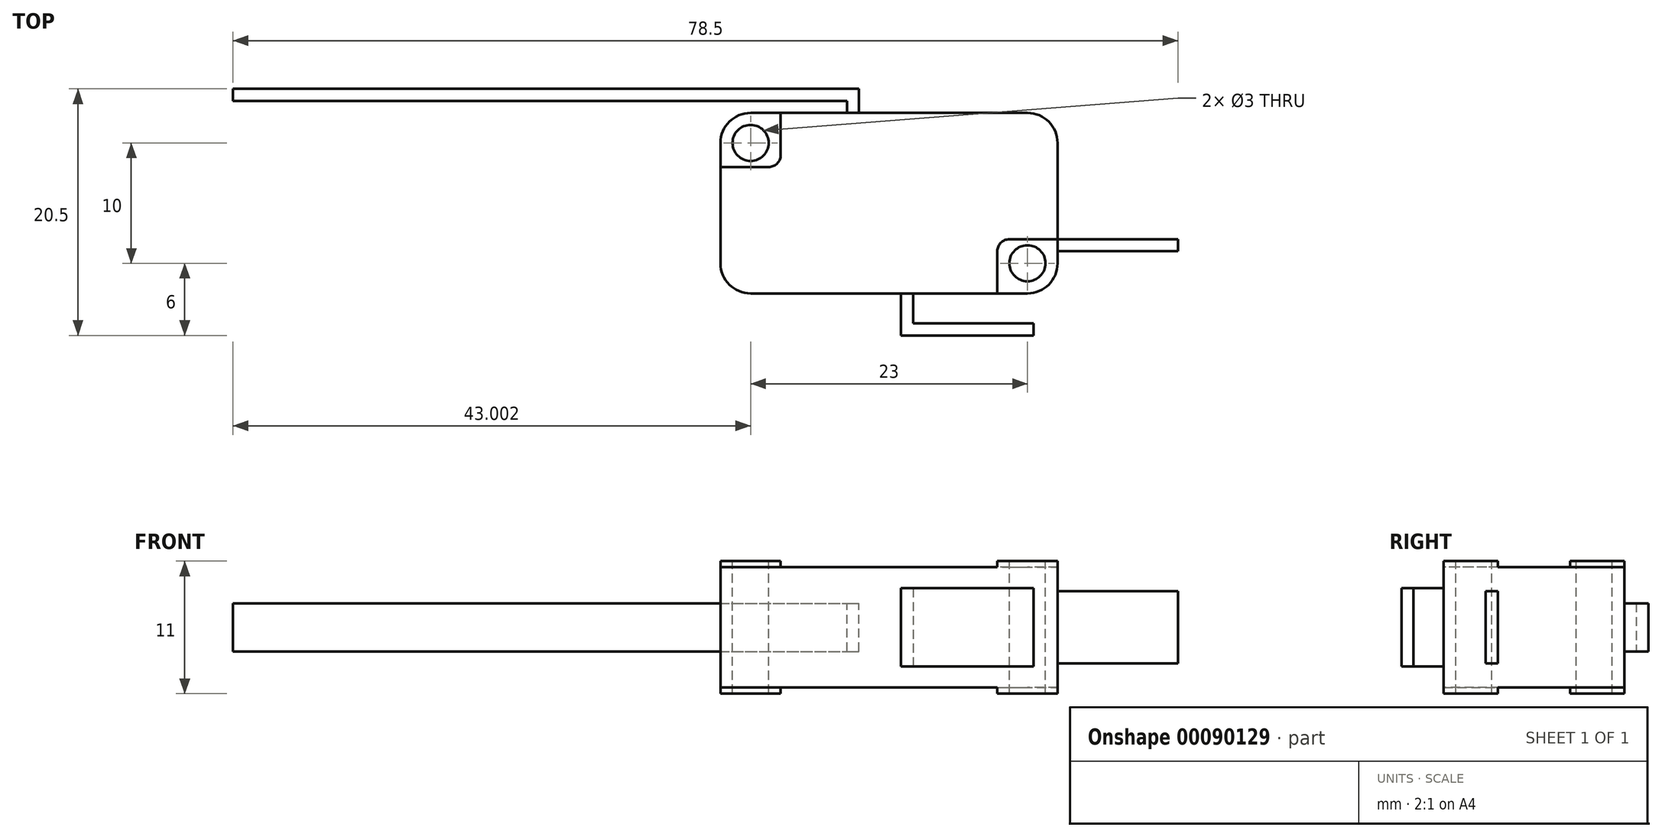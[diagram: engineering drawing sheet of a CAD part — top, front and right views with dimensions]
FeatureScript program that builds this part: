
annotation { "Feature Type Name" : "Feature", "Feature Type Description" : "" }
export const myFeature = defineFeature(function(context is Context, id is Id, definition is map)
    precondition{}
    {
        {
            var Q0;
            Q0=qCreatedBy(makeId("Top.planeOp"),FACE);
            var sketch = newSketch(context, id + "F0", { "sketchPlane" : qUnion([Q0])});
            skLineSegment(sketch, "E0.bottom", {"start": v(-11.85, 4.57) * mm, "end": v(11.15, 4.57) * mm});
            skLineSegment(sketch, "E0.top", {"start": v(-11.85, -10.43) * mm, "end": v(11.15, -10.43) * mm});
            skLineSegment(sketch, "E0.left", {"start": v(-14.35, 2.07) * mm, "end": v(-14.35, -7.93) * mm});
            skLineSegment(sketch, "E0.right", {"start": v(13.65, 2.07) * mm, "end": v(13.65, -7.93) * mm});
            skPoint(sketch, "E1.visualSharp", {"position": v(-14.35, 4.57) * mm});
            skArc(sketch, "E1.filletArc", {"start": v(-11.85, 4.57) * mm, "mid": v(-13.62, 3.84) * mm, "end": v(-14.35, 2.07) * mm});
            skPoint(sketch, "E2.visualSharp", {"position": v(13.65, 4.57) * mm});
            skArc(sketch, "E2.filletArc", {"start": v(13.65, 2.07) * mm, "mid": v(12.92, 3.84) * mm, "end": v(11.15, 4.57) * mm});
            skPoint(sketch, "E3.visualSharp", {"position": v(13.65, -10.43) * mm});
            skArc(sketch, "E3.filletArc", {"start": v(11.15, -10.43) * mm, "mid": v(12.92, -9.7) * mm, "end": v(13.65, -7.93) * mm});
            skPoint(sketch, "E4.visualSharp", {"position": v(-14.35, -10.43) * mm});
            skArc(sketch, "E4.filletArc", {"start": v(-14.35, -7.93) * mm, "mid": v(-13.62, -9.7) * mm, "end": v(-11.85, -10.43) * mm});
            skSolve(sketch);
        }
        {
            var Q0;
            Q0 = qSketchRegion(id + "F0", true);
            extrude(context, id + "F1", {"entities" : qUnion([Q0]), "depth" : 10 * mm});
        }
        {
            var Q0;
            Q0=makeQuery(id+"F1.opExtrude","CAP_FACE",FACE,{"disambiguationData":[OSD([sQuery(id+"F0.wireOp",EDGE,"E0.bottom"),sQuery(id+"F0.wireOp",EDGE,"E0.top"),sQuery(id+"F0.wireOp",EDGE,"E0.left"),sQuery(id+"F0.wireOp",EDGE,"E0.right"),sQuery(id+"F0.wireOp",EDGE,"E1.filletArc"),sQuery(id+"F0.wireOp",EDGE,"E2.filletArc"),sQuery(id+"F0.wireOp",EDGE,"E3.filletArc"),sQuery(id+"F0.wireOp",EDGE,"E4.filletArc")])],"isStart":false});
            var sketch = newSketch(context, id + "F2", { "sketchPlane" : qUnion([Q0])});
            skCircle(sketch, "E5", {"center": v(-11.85, 2.07) * mm, "radius": 1.5 * mm});
            skCircle(sketch, "E6", {"center": v(11.15, -7.93) * mm, "radius": 1.5 * mm});
            skSolve(sketch);
        }
        {
            var Q0;
            Q0 = qSketchRegion(id + "F2", true);
            extrude(context, id + "F3", {"entities" : qUnion([Q0]), "operationType" : NewBodyOperationType.REMOVE, "oppositeDirection" : true, "depth" : 15 * mm});
        }
        {
            var Q0;
            Q0=makeQuery(id+"F1.opExtrude","CAP_FACE",FACE,{"disambiguationData":[OSD([sQuery(id+"F0.wireOp",EDGE,"E0.bottom"),sQuery(id+"F0.wireOp",EDGE,"E0.top"),sQuery(id+"F0.wireOp",EDGE,"E0.left"),sQuery(id+"F0.wireOp",EDGE,"E0.right"),sQuery(id+"F0.wireOp",EDGE,"E1.filletArc"),sQuery(id+"F0.wireOp",EDGE,"E2.filletArc"),sQuery(id+"F0.wireOp",EDGE,"E3.filletArc"),sQuery(id+"F0.wireOp",EDGE,"E4.filletArc")])],"isStart":false});
            var sketch = newSketch(context, id + "F4", { "sketchPlane" : qUnion([Q0])});
            skPoint(sketch, "E7", {"position": v(-9.35, 4.57) * mm});
            skPoint(sketch, "E8", {"position": v(-9.35, 0.07) * mm});
            skLineSegment(sketch, "E9.bottom", {"start": v(-9.35, 4.57) * mm, "end": v(-14.35, 4.57) * mm});
            skLineSegment(sketch, "E9.top", {"start": v(-10.35, 0.07) * mm, "end": v(-14.35, 0.07) * mm});
            skLineSegment(sketch, "E9.left", {"start": v(-9.35, 4.57) * mm, "end": v(-9.35, 1.07) * mm});
            skLineSegment(sketch, "E9.right", {"start": v(-14.35, 4.57) * mm, "end": v(-14.35, 0.07) * mm});
            skPoint(sketch, "E10", {"position": v(8.65, -10.43) * mm});
            skPoint(sketch, "E11", {"position": v(8.65, -5.93) * mm});
            skLineSegment(sketch, "E12.bottom", {"start": v(9.65, -5.93) * mm, "end": v(13.66, -5.93) * mm});
            skLineSegment(sketch, "E12.top", {"start": v(8.65, -10.43) * mm, "end": v(13.66, -10.43) * mm});
            skLineSegment(sketch, "E12.left", {"start": v(8.65, -6.93) * mm, "end": v(8.65, -10.43) * mm});
            skLineSegment(sketch, "E12.right", {"start": v(13.66, -5.93) * mm, "end": v(13.66, -10.43) * mm});
            skArc(sketch, "E13.filletArc", {"start": v(9.65, -5.93) * mm, "mid": v(8.95, -6.22) * mm, "end": v(8.65, -6.93) * mm});
            skArc(sketch, "E14.filletArc", {"start": v(-10.35, 0.07) * mm, "mid": v(-9.64, 0.36) * mm, "end": v(-9.35, 1.07) * mm});
            skSolve(sketch);
        }
        {
            var Q0;
            {var subQ3=sQuery(id+"F4.wireOp",EDGE,"E9.top");Q0=makeQuery(id+"F4.imprint","IMPRINT",FACE,{"disambiguationData":[TD([[makeQuery(id+"F4.imprint","IMPRINT",EDGE,{"derivedFrom":subQ3}),-1.0]])]});}
            var Q1;
            {var subQ3=sQuery(id+"F4.wireOp",EDGE,"E12.left");Q1=makeQuery(id+"F4.imprint","IMPRINT",FACE,{"disambiguationData":[TD([[makeQuery(id+"F4.imprint","IMPRINT",EDGE,{"derivedFrom":subQ3}),1.0]])]});}
            extrude(context, id + "F5", {"entities" : qUnion([Q0, Q1]), "operationType" : NewBodyOperationType.ADD, "depth" : 0.5 * mm});
        }
        {
            var Q0;
            Q0=makeQuery(id+"F1.opExtrude","CAP_FACE",FACE,{"disambiguationData":[OSD([sQuery(id+"F0.wireOp",EDGE,"E0.bottom"),sQuery(id+"F0.wireOp",EDGE,"E0.top"),sQuery(id+"F0.wireOp",EDGE,"E0.left"),sQuery(id+"F0.wireOp",EDGE,"E0.right"),sQuery(id+"F0.wireOp",EDGE,"E1.filletArc"),sQuery(id+"F0.wireOp",EDGE,"E2.filletArc"),sQuery(id+"F0.wireOp",EDGE,"E3.filletArc"),sQuery(id+"F0.wireOp",EDGE,"E4.filletArc")])],"isStart":true});
            var sketch = newSketch(context, id + "F6", { "sketchPlane" : qUnion([Q0])});
            skLineSegment(sketch, "E15.bottom", {"start": v(-14.35, -0.07) * mm, "end": v(-10.35, -0.07) * mm});
            skLineSegment(sketch, "E15.top", {"start": v(-14.35, -4.57) * mm, "end": v(-9.35, -4.57) * mm});
            skLineSegment(sketch, "E15.left", {"start": v(-14.35, -0.07) * mm, "end": v(-14.35, -4.57) * mm});
            skLineSegment(sketch, "E15.right", {"start": v(-9.35, -1.07) * mm, "end": v(-9.35, -4.57) * mm});
            skLineSegment(sketch, "E16.bottom", {"start": v(8.65, 10.43) * mm, "end": v(13.65, 10.43) * mm});
            skLineSegment(sketch, "E16.top", {"start": v(9.65, 5.93) * mm, "end": v(13.65, 5.93) * mm});
            skLineSegment(sketch, "E16.left", {"start": v(8.65, 10.43) * mm, "end": v(8.65, 6.93) * mm});
            skLineSegment(sketch, "E16.right", {"start": v(13.65, 10.43) * mm, "end": v(13.65, 5.93) * mm});
            skPoint(sketch, "E17.visualSharp", {"position": v(8.65, 5.93) * mm});
            skArc(sketch, "E17.filletArc", {"start": v(8.65, 6.93) * mm, "mid": v(8.95, 6.22) * mm, "end": v(9.65, 5.93) * mm});
            skPoint(sketch, "E18.visualSharp", {"position": v(-9.35, -0.07) * mm});
            skArc(sketch, "E18.filletArc", {"start": v(-9.35, -1.07) * mm, "mid": v(-9.64, -0.36) * mm, "end": v(-10.35, -0.07) * mm});
            skSolve(sketch);
        }
        {
            var Q0;
            {var subQ3=sQuery(id+"F6.wireOp",EDGE,"E15.bottom");Q0=makeQuery(id+"F6.imprint","IMPRINT",FACE,{"disambiguationData":[TD([[makeQuery(id+"F6.imprint","IMPRINT",EDGE,{"derivedFrom":subQ3}),-1.0]])]});}
            var Q1;
            {var subQ3=sQuery(id+"F6.wireOp",EDGE,"E16.top");Q1=makeQuery(id+"F6.imprint","IMPRINT",FACE,{"disambiguationData":[TD([[makeQuery(id+"F6.imprint","IMPRINT",EDGE,{"derivedFrom":subQ3}),1.0]])]});}
            extrude(context, id + "F7", {"entities" : qUnion([Q0, Q1]), "operationType" : NewBodyOperationType.ADD, "depth" : 0.5 * mm});
        }
        {
            var Q0;
            {var subQ0=sQuery(id+"F0.wireOp",EDGE,"E0.right");Q0=makeQuery(id+"F7.boolean.opBoolean","MERGE",FACE,{"derivedFrom":[makeQuery(id+"F5.boolean.opBoolean","MERGE",FACE,{"derivedFrom":[makeQuery(id+"F1.opExtrude","SWEPT_FACE",FACE,{"disambiguationData":[OSD([subQ0])]}),makeQuery(id+"F5.opExtrude","SWEPT_FACE",FACE,{"disambiguationData":[OSD([subQ0])]})]}),makeQuery(id+"F7.opExtrude","SWEPT_FACE",FACE,{"disambiguationData":[OSD([sQuery(id+"F6.wireOp",EDGE,"E16.right")])]})]});}
            var sketch = newSketch(context, id + "F8", { "sketchPlane" : qUnion([Q0])});
            skLineSegment(sketch, "E19.bottom", {"start": v(-5.93, 8) * mm, "end": v(-6.93, 8) * mm});
            skLineSegment(sketch, "E19.top", {"start": v(-5.93, 2) * mm, "end": v(-6.93, 2) * mm});
            skLineSegment(sketch, "E19.left", {"start": v(-5.93, 8) * mm, "end": v(-5.93, 2) * mm});
            skLineSegment(sketch, "E19.right", {"start": v(-6.93, 8) * mm, "end": v(-6.93, 2) * mm});
            skSolve(sketch);
        }
        {
            var Q0;
            Q0=makeQuery(id+"F8.imprint","IMPRINT",FACE,{"disambiguationData":[TD([[makeQuery(id+"F8.imprint","IMPRINT",EDGE,{"derivedFrom":sQuery(id+"F8.wireOp",EDGE,"E19.bottom")}),1.0]])]});
            extrude(context, id + "F9", {"entities" : qUnion([Q0]), "operationType" : NewBodyOperationType.ADD, "depth" : 10 * mm});
        }
        {
            var Q0;
            Q0=makeQuery(id+"F7.boolean.opBoolean","MERGE",FACE,{"derivedFrom":[makeQuery(id+"F5.boolean.opBoolean","MERGE",FACE,{"derivedFrom":[makeQuery(id+"F1.opExtrude","SWEPT_FACE",FACE,{"disambiguationData":[OSD([sQuery(id+"F0.wireOp",EDGE,"E0.top")])]}),makeQuery(id+"F5.opExtrude","SWEPT_FACE",FACE,{"disambiguationData":[OSD([sQuery(id+"F4.wireOp",EDGE,"E12.top")])]})]}),makeQuery(id+"F7.opExtrude","SWEPT_FACE",FACE,{"disambiguationData":[OSD([sQuery(id+"F6.wireOp",EDGE,"E16.bottom")])]})]});
            var sketch = newSketch(context, id + "F10", { "sketchPlane" : qUnion([Q0])});
            skLineSegment(sketch, "E20.bottom", {"start": v(0.65, 8.25) * mm, "end": v(1.65, 8.25) * mm});
            skLineSegment(sketch, "E20.top", {"start": v(0.65, 1.75) * mm, "end": v(1.65, 1.75) * mm});
            skLineSegment(sketch, "E20.left", {"start": v(0.65, 8.25) * mm, "end": v(0.65, 1.75) * mm});
            skLineSegment(sketch, "E20.right", {"start": v(1.65, 8.25) * mm, "end": v(1.65, 1.75) * mm});
            skSolve(sketch);
        }
        {
            var Q0;
            Q0=makeQuery(id+"F10.imprint","IMPRINT",FACE,{"disambiguationData":[TD([[makeQuery(id+"F10.imprint","IMPRINT",EDGE,{"derivedFrom":sQuery(id+"F10.wireOp",EDGE,"E20.bottom")}),-1.0]])]});
            extrude(context, id + "F11", {"entities" : qUnion([Q0]), "operationType" : NewBodyOperationType.ADD, "depth" : 3.5 * mm});
        }
        {
            var Q0;
            Q0=makeQuery(id+"F11.opExtrude","SWEPT_FACE",FACE,{"disambiguationData":[OSD([sQuery(id+"F10.wireOp",EDGE,"E20.right")])]});
            var sketch = newSketch(context, id + "F12", { "sketchPlane" : qUnion([Q0])});
            skLineSegment(sketch, "E21.bottom", {"start": v(-13.93, 8.25) * mm, "end": v(-12.93, 8.25) * mm});
            skLineSegment(sketch, "E21.top", {"start": v(-13.93, 1.75) * mm, "end": v(-12.93, 1.75) * mm});
            skLineSegment(sketch, "E21.left", {"start": v(-13.93, 8.25) * mm, "end": v(-13.93, 1.75) * mm});
            skLineSegment(sketch, "E21.right", {"start": v(-12.93, 8.25) * mm, "end": v(-12.93, 1.75) * mm});
            skSolve(sketch);
        }
        {
            var Q0;
            Q0 = qSketchRegion(id + "F12", true);
            extrude(context, id + "F13", {"entities" : qUnion([Q0]), "operationType" : NewBodyOperationType.ADD, "depth" : 10 * mm});
        }
        {
            var Q0;
            Q0=makeQuery(id+"F7.boolean.opBoolean","MERGE",FACE,{"derivedFrom":[makeQuery(id+"F5.boolean.opBoolean","MERGE",FACE,{"derivedFrom":[makeQuery(id+"F1.opExtrude","SWEPT_FACE",FACE,{"disambiguationData":[OSD([sQuery(id+"F0.wireOp",EDGE,"E0.bottom")])]}),makeQuery(id+"F5.opExtrude","SWEPT_FACE",FACE,{"disambiguationData":[OSD([sQuery(id+"F4.wireOp",EDGE,"E9.bottom")])]})]}),makeQuery(id+"F7.opExtrude","SWEPT_FACE",FACE,{"disambiguationData":[OSD([sQuery(id+"F6.wireOp",EDGE,"E15.top")])]})]});
            var sketch = newSketch(context, id + "F14", { "sketchPlane" : qUnion([Q0])});
            skLineSegment(sketch, "E22.bottom", {"start": v(3.85, 3) * mm, "end": v(2.85, 3) * mm});
            skLineSegment(sketch, "E22.top", {"start": v(3.85, 7) * mm, "end": v(2.85, 7) * mm});
            skLineSegment(sketch, "E22.left", {"start": v(3.85, 3) * mm, "end": v(3.85, 7) * mm});
            skLineSegment(sketch, "E22.right", {"start": v(2.85, 3) * mm, "end": v(2.85, 7) * mm});
            skSolve(sketch);
        }
        {
            var Q0;
            Q0 = qSketchRegion(id + "F14", true);
            extrude(context, id + "F15", {"entities" : qUnion([Q0]), "operationType" : NewBodyOperationType.ADD, "depth" : 2 * mm});
        }
        {
            var Q0;
            Q0=makeQuery(id+"F15.opExtrude","SWEPT_FACE",FACE,{"disambiguationData":[OSD([sQuery(id+"F14.wireOp",EDGE,"E22.left")])]});
            var sketch = newSketch(context, id + "F16", { "sketchPlane" : qUnion([Q0])});
            skLineSegment(sketch, "E23", {"start": v(-5.57, 7) * mm, "end": v(-5.57, 3) * mm});
            skSolve(sketch);
        }
        {
            var Q0;
            Q0 = qSketchRegion(id + "F16", true);
            var Q1;
            {var subQ0=sQuery(id+"F16.wireOp",EDGE,"E23");Q1=makeQuery(id+"F16.imprint","IMPRINT",FACE,{"disambiguationData":[TD([[makeQuery(id+"F16.imprint","IMPRINT",EDGE,{"derivedFrom":subQ0}),-1.0]])]});}
            extrude(context, id + "F17", {"entities" : qUnion([Q0, Q1]), "operationType" : NewBodyOperationType.ADD, "depth" : 51 * mm});
        }
    });
